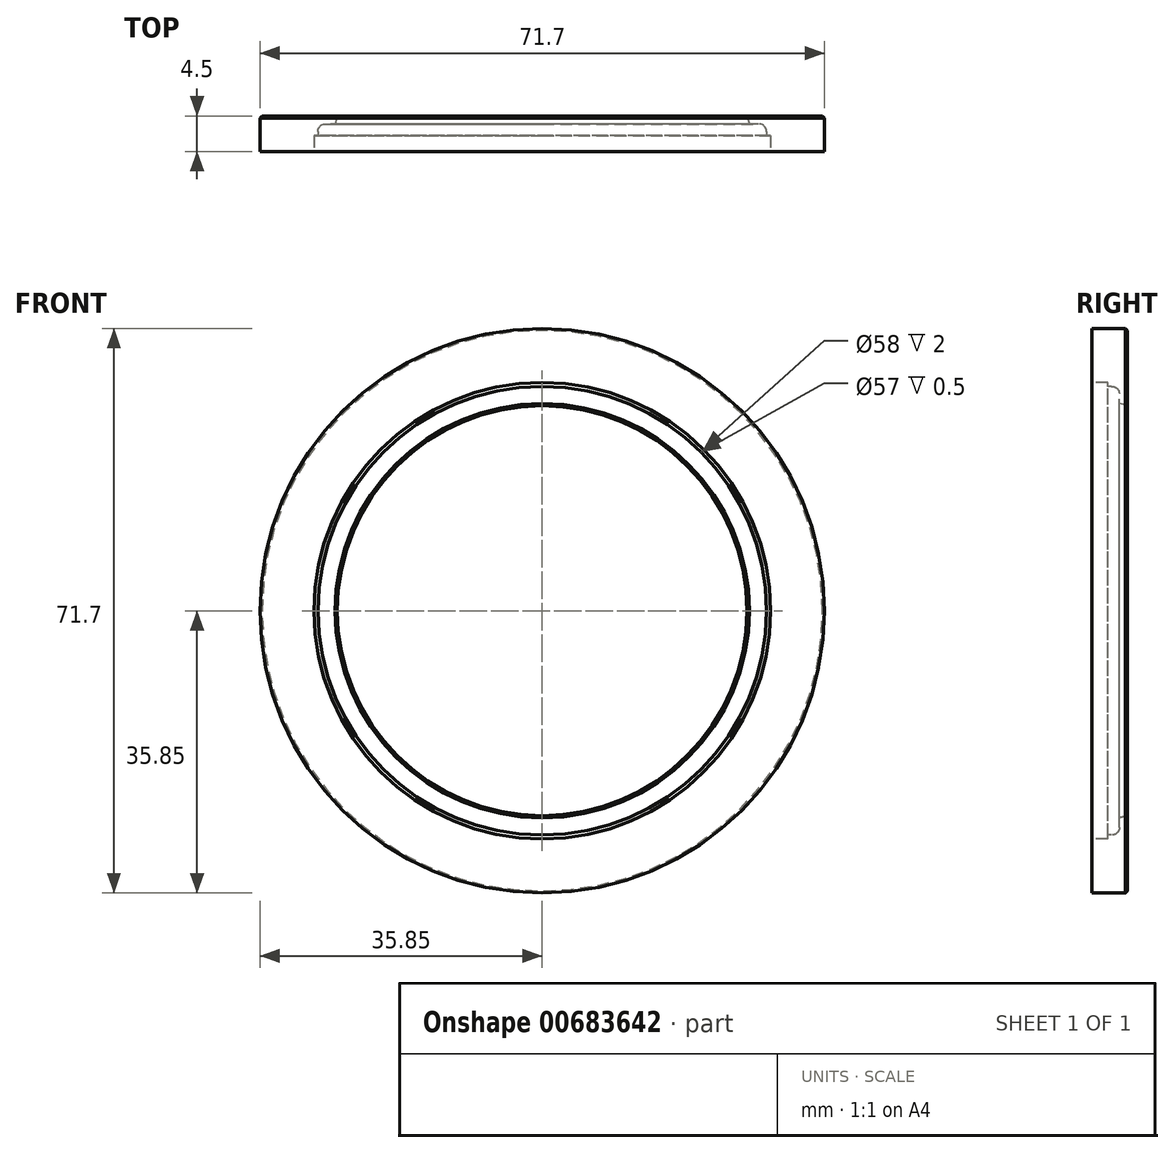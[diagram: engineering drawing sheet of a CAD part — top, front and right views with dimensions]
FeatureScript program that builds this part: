
annotation { "Feature Type Name" : "Feature", "Feature Type Description" : "" }
export const myFeature = defineFeature(function(context is Context, id is Id, definition is map)
    precondition{}
    {
        {
            var Q0;
            Q0=qCreatedBy(makeId("Right.planeOp"),FACE);
            var sketch = newSketch(context, id + "F0", { "sketchPlane" : qUnion([Q0])});
            skLineSegment(sketch, "E0", {"start": v(-11.42, 0) * mm, "end": v(12.49, 0) * mm, "construction": true});
            skLineSegment(sketch, "E1", {"start": v(0, 35.85) * mm, "end": v(0, 29) * mm});
            skLineSegment(sketch, "E2", {"start": v(0, 29) * mm, "end": v(2, 29) * mm});
            skLineSegment(sketch, "E3", {"start": v(2, 29) * mm, "end": v(2, 28.5) * mm});
            skLineSegment(sketch, "E4", {"start": v(2, 28.5) * mm, "end": v(2.5, 28.5) * mm});
            skLineSegment(sketch, "E5", {"start": v(3.5, 27.5) * mm, "end": v(3.5, 26.3) * mm});
            skLineSegment(sketch, "E6", {"start": v(3.5, 26.3) * mm, "end": v(4.5, 26.04) * mm});
            skLineSegment(sketch, "E7", {"start": v(4.5, 26.04) * mm, "end": v(4.5, 35.6) * mm});
            skLineSegment(sketch, "E8", {"start": v(4.25, 35.85) * mm, "end": v(0, 35.85) * mm});
            skLineSegment(sketch, "E9", {"start": v(4.25, 35.85) * mm, "end": v(4.5, 35.6) * mm});
            skPoint(sketch, "E10.orphan", {"position": v(4.5, 35.85) * mm});
            skPoint(sketch, "E11.visualSharp", {"position": v(3.5, 28.5) * mm});
            skArc(sketch, "E11.filletArc", {"start": v(3.5, 27.5) * mm, "mid": v(3.2, 28.2) * mm, "end": v(2.5, 28.5) * mm});
            skSolve(sketch);
        }
        {
            var Q0;
            Q0=makeQuery(id+"F0.imprint","IMPRINT",FACE,{"disambiguationData":[TD([[makeQuery(id+"F0.imprint","IMPRINT",EDGE,{"derivedFrom":sQuery(id+"F0.wireOp",EDGE,"E1")}),1.0]])]});
            var Q1;
            Q1=sQuery(id+"F0.wireOp",EDGE,"E0");
            revolve(context, id + "F1", {"entities" : qUnion([Q0]), "axis" : qUnion([Q1]), "revolveType" : RevolveType.FULL});
        }
    });
